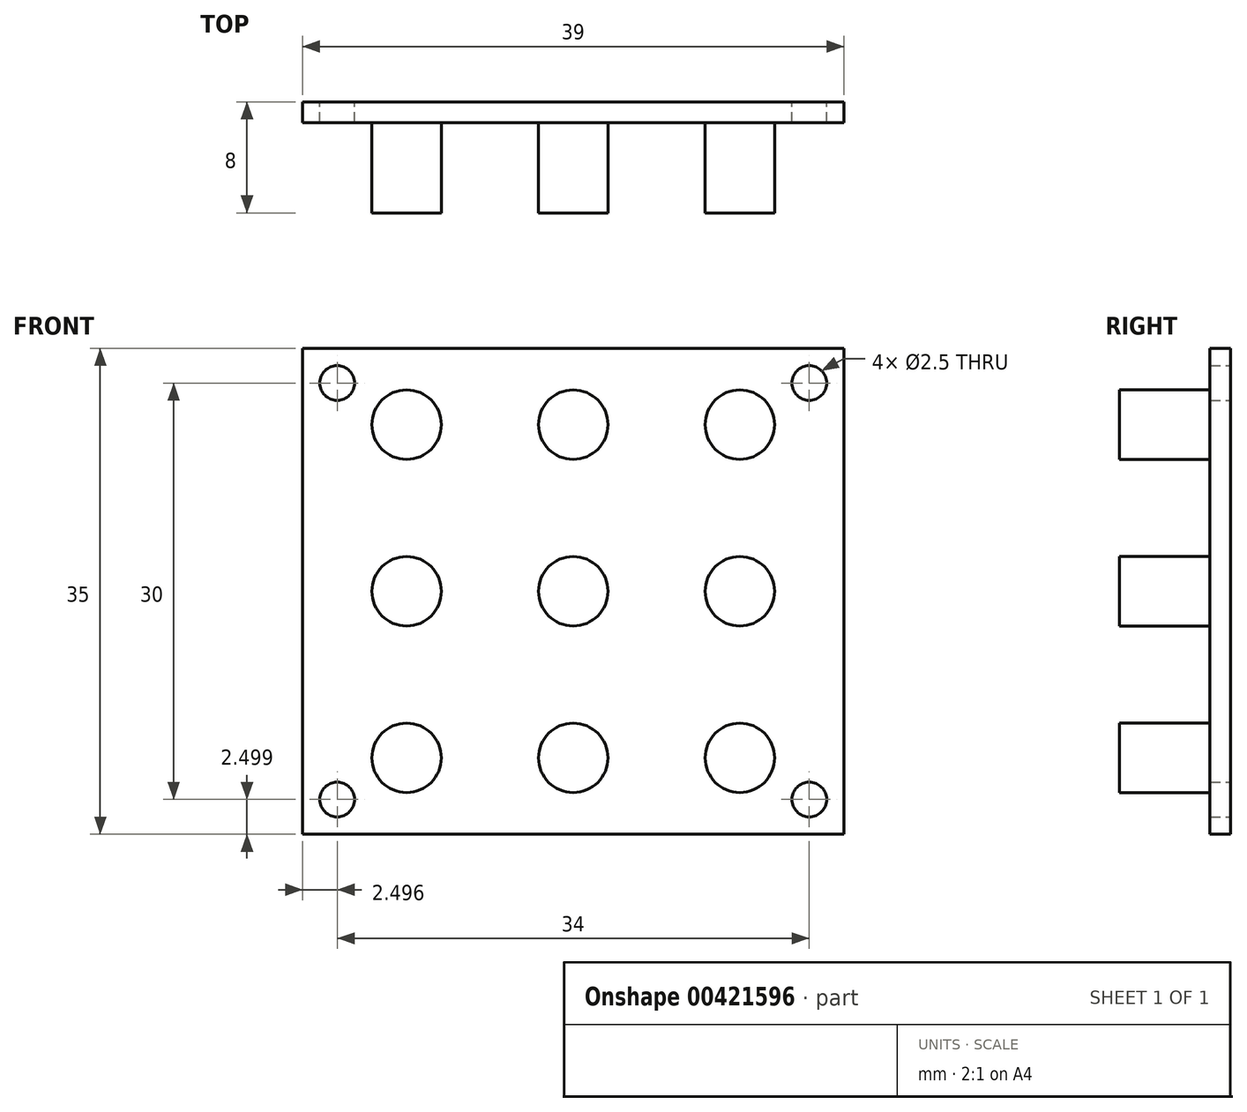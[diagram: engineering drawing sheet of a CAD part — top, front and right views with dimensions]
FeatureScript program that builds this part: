
annotation { "Feature Type Name" : "Feature", "Feature Type Description" : "" }
export const myFeature = defineFeature(function(context is Context, id is Id, definition is map)
    precondition{}
    {
        {
            var Q0;
            Q0=qCreatedBy(makeId("Front.planeOp"),FACE);
            var sketch = newSketch(context, id + "F0", { "sketchPlane" : qUnion([Q0])});
            skLineSegment(sketch, "E0.bottom", {"start": v(-40.54, 54.02) * mm, "end": v(-1.54, 54.02) * mm});
            skLineSegment(sketch, "E0.top", {"start": v(-40.54, 19.02) * mm, "end": v(-1.54, 19.02) * mm});
            skLineSegment(sketch, "E0.left", {"start": v(-40.54, 54.02) * mm, "end": v(-40.54, 19.02) * mm});
            skLineSegment(sketch, "E0.right", {"start": v(-1.54, 54.02) * mm, "end": v(-1.54, 19.02) * mm});
            skCircle(sketch, "E1", {"center": v(-38.04, 51.52) * mm, "radius": 1.25 * mm});
            skCircle(sketch, "E2", {"center": v(-4.04, 51.52) * mm, "radius": 1.25 * mm});
            skCircle(sketch, "E3.MirrorC", {"center": v(-38.04, 21.52) * mm, "radius": 1.25 * mm});
            skCircle(sketch, "E4.MirrorC", {"center": v(-4.04, 21.52) * mm, "radius": 1.25 * mm});
            skCircle(sketch, "E5", {"center": v(-33.04, 48.52) * mm, "radius": 2.5 * mm});
            skCircle(sketch, "E6", {"center": v(-21.04, 48.52) * mm, "radius": 2.5 * mm});
            skCircle(sketch, "E7", {"center": v(-9.04, 48.52) * mm, "radius": 2.5 * mm});
            skCircle(sketch, "E8", {"center": v(-33.04, 36.52) * mm, "radius": 2.5 * mm});
            skCircle(sketch, "E9", {"center": v(-21.04, 36.52) * mm, "radius": 2.5 * mm});
            skCircle(sketch, "E10", {"center": v(-9.04, 36.52) * mm, "radius": 2.5 * mm});
            skCircle(sketch, "E11", {"center": v(-33.04, 24.52) * mm, "radius": 2.5 * mm});
            skCircle(sketch, "E12", {"center": v(-21.04, 24.52) * mm, "radius": 2.5 * mm});
            skCircle(sketch, "E13", {"center": v(-9.04, 24.52) * mm, "radius": 2.5 * mm});
            skSolve(sketch);
        }
        {
            var Q0;
            Q0=makeQuery(id+"F0.imprint","IMPRINT",FACE,{"disambiguationData":[TD([[makeQuery(id+"F0.imprint","IMPRINT",EDGE,{"derivedFrom":sQuery(id+"F0.wireOp",EDGE,"E0.bottom")}),-1.0]])]});
            extrude(context, id + "F1", {"entities" : qUnion([Q0]), "depth" : 1.5 * mm, "offsetDistance" : 25 * mm});
        }
        {
            var Q0;
            Q0=makeQuery(id+"F0.imprint","IMPRINT",FACE,{"disambiguationData":[TD([[makeQuery(id+"F0.imprint","IMPRINT",EDGE,{"derivedFrom":sQuery(id+"F0.wireOp",EDGE,"E5")}),1.0]])]});
            var Q1;
            Q1=makeQuery(id+"F0.imprint","IMPRINT",FACE,{"disambiguationData":[TD([[makeQuery(id+"F0.imprint","IMPRINT",EDGE,{"derivedFrom":sQuery(id+"F0.wireOp",EDGE,"E6")}),1.0]])]});
            var Q2;
            Q2=makeQuery(id+"F0.imprint","IMPRINT",FACE,{"disambiguationData":[TD([[makeQuery(id+"F0.imprint","IMPRINT",EDGE,{"derivedFrom":sQuery(id+"F0.wireOp",EDGE,"E7")}),1.0]])]});
            var Q3;
            Q3=makeQuery(id+"F0.imprint","IMPRINT",FACE,{"disambiguationData":[TD([[makeQuery(id+"F0.imprint","IMPRINT",EDGE,{"derivedFrom":sQuery(id+"F0.wireOp",EDGE,"E8")}),1.0]])]});
            var Q4;
            Q4=makeQuery(id+"F0.imprint","IMPRINT",FACE,{"disambiguationData":[TD([[makeQuery(id+"F0.imprint","IMPRINT",EDGE,{"derivedFrom":sQuery(id+"F0.wireOp",EDGE,"E9")}),1.0]])]});
            var Q5;
            Q5=makeQuery(id+"F0.imprint","IMPRINT",FACE,{"disambiguationData":[TD([[makeQuery(id+"F0.imprint","IMPRINT",EDGE,{"derivedFrom":sQuery(id+"F0.wireOp",EDGE,"E10")}),1.0]])]});
            var Q6;
            Q6=makeQuery(id+"F0.imprint","IMPRINT",FACE,{"disambiguationData":[TD([[makeQuery(id+"F0.imprint","IMPRINT",EDGE,{"derivedFrom":sQuery(id+"F0.wireOp",EDGE,"E11")}),1.0]])]});
            var Q7;
            Q7=makeQuery(id+"F0.imprint","IMPRINT",FACE,{"disambiguationData":[TD([[makeQuery(id+"F0.imprint","IMPRINT",EDGE,{"derivedFrom":sQuery(id+"F0.wireOp",EDGE,"E12")}),1.0]])]});
            var Q8;
            Q8=makeQuery(id+"F0.imprint","IMPRINT",FACE,{"disambiguationData":[TD([[makeQuery(id+"F0.imprint","IMPRINT",EDGE,{"derivedFrom":sQuery(id+"F0.wireOp",EDGE,"E13")}),1.0]])]});
            extrude(context, id + "F2", {"entities" : qUnion([Q0, Q1, Q2, Q3, Q4, Q5, Q6, Q7, Q8]), "operationType" : NewBodyOperationType.ADD, "depth" : 8 * mm, "offsetDistance" : 25 * mm});
        }
    });
